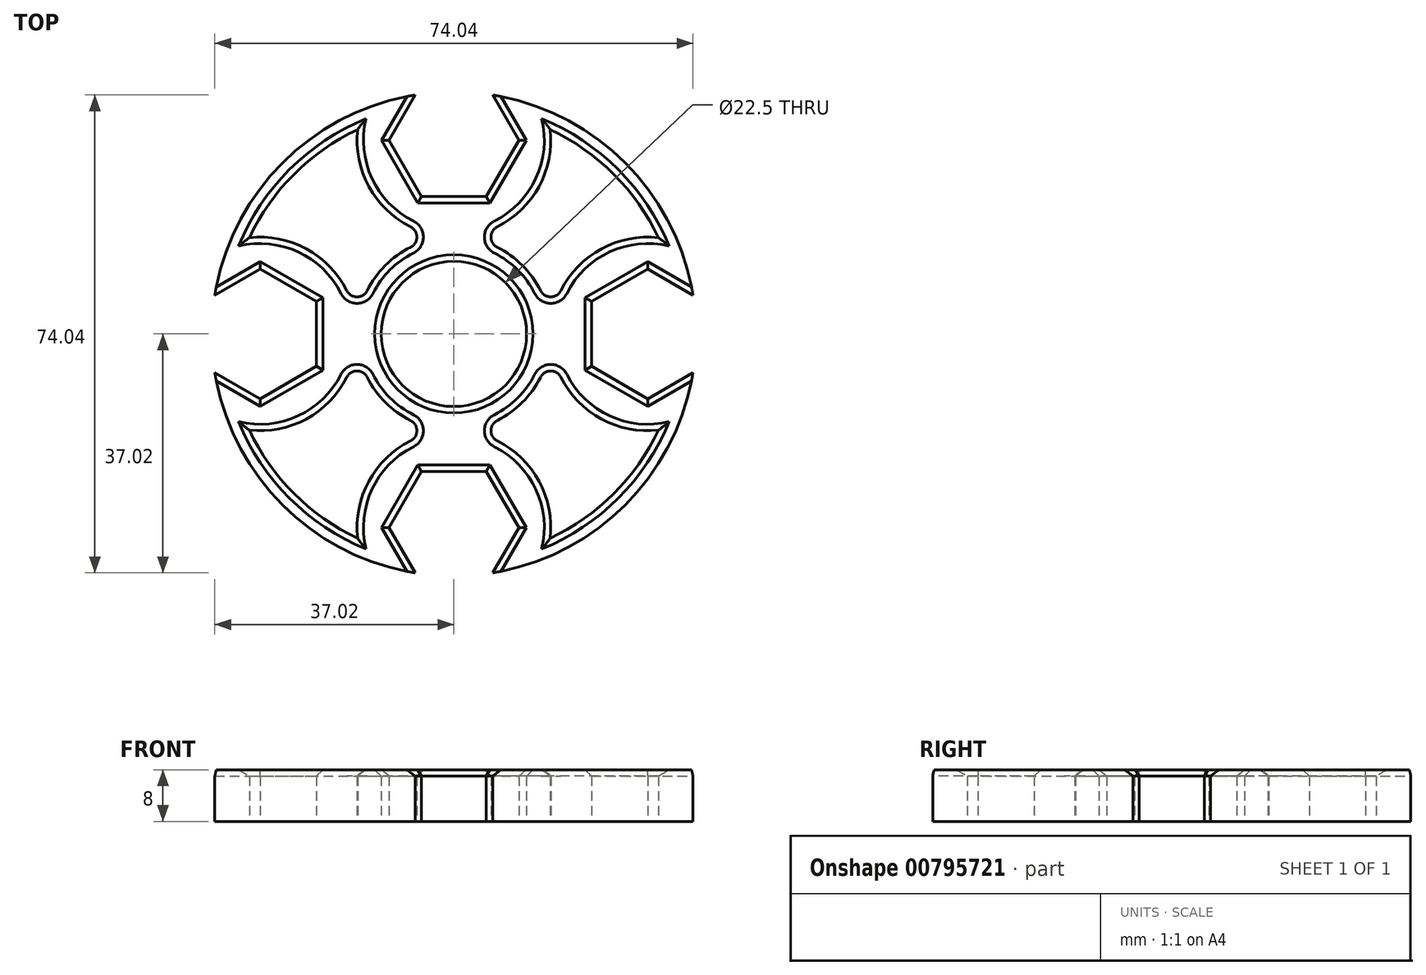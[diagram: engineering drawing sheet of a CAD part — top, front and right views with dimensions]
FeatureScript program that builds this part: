
annotation { "Feature Type Name" : "Feature", "Feature Type Description" : "" }
export const myFeature = defineFeature(function(context is Context, id is Id, definition is map)
    precondition{}
    {
        {
            var Q0;
            Q0=qCreatedBy(makeId("Top.planeOp"),FACE);
            var sketch = newSketch(context, id + "F0", { "sketchPlane" : qUnion([Q0])});
            skCircle(sketch, "E0", {"center": v(0, 0) * mm, "radius": 35 * mm});
            skLineSegment(sketch, "E1.bottom", {"start": v(-35, 35) * mm, "end": v(35, 35) * mm});
            skLineSegment(sketch, "E1.top", {"start": v(-35, -35) * mm, "end": v(35, -35) * mm});
            skLineSegment(sketch, "E1.left", {"start": v(-35, 35) * mm, "end": v(-35, -35) * mm});
            skLineSegment(sketch, "E1.right", {"start": v(35, 35) * mm, "end": v(35, -35) * mm});
            skCircle(sketch, "E2", {"center": v(0, 0) * mm, "radius": 15 * mm});
            skLineSegment(sketch, "E3", {"start": v(-35, 0) * mm, "end": v(-15, 0) * mm});
            skLineSegment(sketch, "E4", {"start": v(0, -15) * mm, "end": v(0, -35) * mm});
            skLineSegment(sketch, "E5", {"start": v(35, 0) * mm, "end": v(15, 0) * mm});
            skLineSegment(sketch, "E6", {"start": v(0, 35) * mm, "end": v(0, 15) * mm});
            skLineSegment(sketch, "E7", {"start": v(-25, 0) * mm, "end": v(-35, 0) * mm});
            skLineSegment(sketch, "E8", {"start": v(35, 0) * mm, "end": v(25, 0) * mm});
            skLineSegment(sketch, "E9", {"start": v(0, 35) * mm, "end": v(0, 25) * mm});
            skLineSegment(sketch, "E10", {"start": v(0, -25) * mm, "end": v(0, -35) * mm});
            skCircle(sketch, "E11.cCircle", {"center": v(-30, 0) * mm, "radius": 10.05 * mm, "construction": true});
            skPoint(sketch, "E11.cCircle.perimeterSnap0", {"position": v(-30, 0) * mm});
            skLineSegment(sketch, "E11.0", {"start": v(-30, 10.05) * mm, "end": v(-21.3, 5.02) * mm});
            skPoint(sketch, "E11.0.startSnap0", {"position": v(-30, 0) * mm});
            skLineSegment(sketch, "E11.1", {"start": v(-21.3, 5.03) * mm, "end": v(-21.3, -5.02) * mm});
            skLineSegment(sketch, "E11.2", {"start": v(-21.3, -5.02) * mm, "end": v(-30, -10.05) * mm});
            skLineSegment(sketch, "E11.3", {"start": v(-30, -10.05) * mm, "end": v(-38.7, -5.02) * mm});
            skLineSegment(sketch, "E11.4", {"start": v(-38.7, -5.03) * mm, "end": v(-38.7, 5.02) * mm});
            skLineSegment(sketch, "E11.5", {"start": v(-38.7, 5.02) * mm, "end": v(-30, 10.05) * mm});
            skCircle(sketch, "E12.cCircle", {"center": v(30, 0) * mm, "radius": 10.05 * mm, "construction": true});
            skPoint(sketch, "E12.cCircle.perimeterSnap0", {"position": v(30, 0) * mm});
            skLineSegment(sketch, "E12.0", {"start": v(30, 10.05) * mm, "end": v(38.7, 5.02) * mm});
            skPoint(sketch, "E12.0.startSnap0", {"position": v(30, 0) * mm});
            skLineSegment(sketch, "E12.1", {"start": v(38.7, 5.03) * mm, "end": v(38.7, -5.03) * mm});
            skLineSegment(sketch, "E12.2", {"start": v(38.7, -5.03) * mm, "end": v(30, -10.05) * mm});
            skLineSegment(sketch, "E12.3", {"start": v(30, -10.05) * mm, "end": v(21.3, -5.03) * mm});
            skLineSegment(sketch, "E12.4", {"start": v(21.3, -5.03) * mm, "end": v(21.3, 5.03) * mm});
            skLineSegment(sketch, "E12.5", {"start": v(21.3, 5.03) * mm, "end": v(30, 10.05) * mm});
            skCircle(sketch, "E13.cCircle", {"center": v(0, 30) * mm, "radius": 10.05 * mm, "construction": true});
            skPoint(sketch, "E13.cCircle.perimeterSnap0", {"position": v(0, 30) * mm});
            skLineSegment(sketch, "E13.0", {"start": v(10.05, 30) * mm, "end": v(5.03, 21.3) * mm});
            skPoint(sketch, "E13.0.startSnap0", {"position": v(0, 30) * mm});
            skLineSegment(sketch, "E13.1", {"start": v(5.03, 21.3) * mm, "end": v(-5.02, 21.3) * mm});
            skLineSegment(sketch, "E13.2", {"start": v(-5.02, 21.3) * mm, "end": v(-10.05, 30) * mm});
            skLineSegment(sketch, "E13.3", {"start": v(-10.05, 30) * mm, "end": v(-5.02, 38.7) * mm});
            skLineSegment(sketch, "E13.4", {"start": v(-5.02, 38.7) * mm, "end": v(5.03, 38.7) * mm});
            skLineSegment(sketch, "E13.5", {"start": v(5.03, 38.7) * mm, "end": v(10.05, 30) * mm});
            skCircle(sketch, "E14.cCircle", {"center": v(0, -30) * mm, "radius": 10.05 * mm, "construction": true});
            skPoint(sketch, "E14.cCircle.perimeterSnap0", {"position": v(0, -30) * mm});
            skLineSegment(sketch, "E14.0", {"start": v(10.05, -30) * mm, "end": v(5.03, -38.7) * mm});
            skPoint(sketch, "E14.0.startSnap0", {"position": v(0, -30) * mm});
            skLineSegment(sketch, "E14.1", {"start": v(5.03, -38.7) * mm, "end": v(-5.03, -38.7) * mm});
            skLineSegment(sketch, "E14.2", {"start": v(-5.03, -38.7) * mm, "end": v(-10.05, -30) * mm});
            skLineSegment(sketch, "E14.3", {"start": v(-10.05, -30) * mm, "end": v(-5.03, -21.3) * mm});
            skLineSegment(sketch, "E14.4", {"start": v(-5.03, -21.3) * mm, "end": v(5.02, -21.3) * mm});
            skLineSegment(sketch, "E14.5", {"start": v(5.02, -21.3) * mm, "end": v(10.05, -30) * mm});
            skCircle(sketch, "E15", {"center": v(0, 30) * mm, "radius": 15 * mm});
            skCircle(sketch, "E16", {"center": v(-30, 0) * mm, "radius": 15 * mm});
            skCircle(sketch, "E17", {"center": v(0, -30) * mm, "radius": 15 * mm});
            skCircle(sketch, "E18", {"center": v(30, 0) * mm, "radius": 15 * mm});
            skLineSegment(sketch, "E19", {"start": v(-15, 0) * mm, "end": v(-15, 7.5) * mm});
            skArc(sketch, "E20", {"start": v(-16.58, 6.7) * mm, "mid": v(-15, 5.73) * mm, "end": v(-13.42, 6.7) * mm});
            skLineSegment(sketch, "E21", {"start": v(-15, 0) * mm, "end": v(-15, -7.5) * mm});
            skLineSegment(sketch, "E22", {"start": v(15, 0) * mm, "end": v(15, 7.5) * mm});
            skLineSegment(sketch, "E23", {"start": v(15, 0) * mm, "end": v(15, -7.5) * mm});
            skLineSegment(sketch, "E24", {"start": v(0, 15) * mm, "end": v(-7.5, 15) * mm});
            skLineSegment(sketch, "E25", {"start": v(0, 15) * mm, "end": v(7.5, 15) * mm});
            skLineSegment(sketch, "E26", {"start": v(0, -15) * mm, "end": v(-7.5, -15) * mm});
            skLineSegment(sketch, "E27", {"start": v(0, -15) * mm, "end": v(7.5, -15) * mm});
            skArc(sketch, "E28", {"start": v(6.7, -13.42) * mm, "mid": v(5.73, -15) * mm, "end": v(6.7, -16.58) * mm});
            skArc(sketch, "E29", {"start": v(-6.7, -16.58) * mm, "mid": v(-5.73, -15) * mm, "end": v(-6.7, -13.42) * mm});
            skArc(sketch, "E30", {"start": v(-6.7, 13.42) * mm, "mid": v(-5.73, 15) * mm, "end": v(-6.7, 16.58) * mm});
            skArc(sketch, "E31", {"start": v(-13.42, -6.7) * mm, "mid": v(-15, -5.73) * mm, "end": v(-16.58, -6.7) * mm});
            skArc(sketch, "E32", {"start": v(16.58, -6.7) * mm, "mid": v(15, -5.73) * mm, "end": v(13.42, -6.7) * mm});
            skArc(sketch, "E33", {"start": v(13.42, 6.7) * mm, "mid": v(15, 5.73) * mm, "end": v(16.58, 6.7) * mm});
            skArc(sketch, "E34", {"start": v(6.7, 16.58) * mm, "mid": v(5.73, 15) * mm, "end": v(6.7, 13.42) * mm});
            skCircle(sketch, "E35", {"center": v(0, 0) * mm, "radius": 37.5 * mm});
            skCircle(sketch, "E36", {"center": v(0, 0) * mm, "radius": 11.25 * mm});
            skSolve(sketch);
        }
        {
            var Q0;
            {var subQ1=sQuery(id+"F0.wireOp",EDGE,"E11.0");Q0=makeQuery(id+"F0.imprint","IMPRINT",FACE,{"disambiguationData":[TD([[makeQuery(id+"F0.imprint","IMPRINT",EDGE,{"derivedFrom":subQ1}),1.0]])]});}
            var Q1;
            {var subQ0=sQuery(id+"F0.wireOp",EDGE,"E11.2");Q1=makeQuery(id+"F0.imprint","IMPRINT",FACE,{"disambiguationData":[TD([[makeQuery(id+"F0.imprint","IMPRINT",EDGE,{"derivedFrom":subQ0}),1.0]])]});}
            var Q2;
            {var subQ1=sQuery(id+"F0.wireOp",EDGE,"E0");var subQ5=sQuery(id+"F0.wireOp",EDGE,"E11.3");var subQ6=makeQuery(id+"F0.imprint","INTERSECT",VERTEX,{"derivedFrom":[subQ1,subQ5]});Q2=makeQuery(id+"F0.imprint","IMPRINT",FACE,{"disambiguationData":[TD([[makeQuery(id+"F0.imprint","IMPRINT",EDGE,{"disambiguationData":[TD([[subQ6,-1.0]])],"derivedFrom":subQ1}),-1.0]])]});}
            var Q3;
            {var subQ0=sQuery(id+"F0.wireOp",EDGE,"E11.3");var subQ1=sQuery(id+"F0.wireOp",EDGE,"E1.left");var subQ2=makeQuery(id+"F0.imprint","INTERSECT",VERTEX,{"derivedFrom":[subQ1,subQ0]});Q3=makeQuery(id+"F0.imprint","IMPRINT",FACE,{"disambiguationData":[TD([[makeQuery(id+"F0.imprint","IMPRINT",EDGE,{"disambiguationData":[TD([[subQ2,-1.0]])],"derivedFrom":subQ1}),-1.0]])]});}
            var Q4;
            {var subQ0=sQuery(id+"F0.wireOp",EDGE,"E35");var subQ1=sQuery(id+"F0.wireOp",EDGE,"E1.left");var subQ2=makeQuery(id+"F0.imprint","INTERSECT",VERTEX,{"disambiguationData":[OD(0.0)],"derivedFrom":[subQ1,subQ0]});Q4=makeQuery(id+"F0.imprint","IMPRINT",FACE,{"disambiguationData":[TD([[makeQuery(id+"F0.imprint","IMPRINT",EDGE,{"disambiguationData":[TD([[subQ2,-1.0]])],"derivedFrom":subQ1}),-1.0]])]});}
            var Q5;
            {var subQ0=sQuery(id+"F0.wireOp",EDGE,"E16");var subQ1=sQuery(id+"F0.wireOp",EDGE,"E0");var subQ2=makeQuery(id+"F0.imprint","INTERSECT",VERTEX,{"disambiguationData":[OD(0.0)],"derivedFrom":[subQ1,subQ0]});Q5=makeQuery(id+"F0.imprint","IMPRINT",FACE,{"disambiguationData":[TD([[makeQuery(id+"F0.imprint","IMPRINT",EDGE,{"disambiguationData":[TD([[subQ2,-1.0]])],"derivedFrom":subQ1}),-1.0]])]});}
            var Q6;
            {var subQ0=sQuery(id+"F0.wireOp",EDGE,"E15");var subQ1=sQuery(id+"F0.wireOp",EDGE,"E0");var subQ2=makeQuery(id+"F0.imprint","INTERSECT",VERTEX,{"disambiguationData":[OD(1.0)],"derivedFrom":[subQ1,subQ0]});Q6=makeQuery(id+"F0.imprint","IMPRINT",FACE,{"disambiguationData":[TD([[makeQuery(id+"F0.imprint","IMPRINT",EDGE,{"disambiguationData":[TD([[subQ2,-1.0]])],"derivedFrom":subQ1}),-1.0]])]});}
            var Q7;
            {var subQ0=sQuery(id+"F0.wireOp",EDGE,"E16");var subQ1=sQuery(id+"F0.wireOp",EDGE,"E0");var subQ2=makeQuery(id+"F0.imprint","INTERSECT",VERTEX,{"disambiguationData":[OD(1.0)],"derivedFrom":[subQ1,subQ0]});Q7=makeQuery(id+"F0.imprint","IMPRINT",FACE,{"disambiguationData":[TD([[makeQuery(id+"F0.imprint","IMPRINT",EDGE,{"disambiguationData":[TD([[subQ2,-1.0]])],"derivedFrom":subQ1}),-1.0]])]});}
            var Q8;
            {var subQ1=sQuery(id+"F0.wireOp",EDGE,"E16");var subQ3=sQuery(id+"F0.wireOp",EDGE,"E31");var subQ4=makeQuery(id+"F0.imprint","INTERSECT",VERTEX,{"derivedFrom":[subQ1,subQ3]});Q8=makeQuery(id+"F0.imprint","IMPRINT",FACE,{"disambiguationData":[TD([[makeQuery(id+"F0.imprint","IMPRINT",EDGE,{"disambiguationData":[TD([[subQ4,1.0]])],"derivedFrom":subQ3}),-1.0]])]});}
            var Q9;
            {var subQ1=sQuery(id+"F0.wireOp",EDGE,"E2");var subQ3=sQuery(id+"F0.wireOp",EDGE,"E31");var subQ4=makeQuery(id+"F0.imprint","INTERSECT",VERTEX,{"derivedFrom":[subQ1,subQ3]});Q9=makeQuery(id+"F0.imprint","IMPRINT",FACE,{"disambiguationData":[TD([[makeQuery(id+"F0.imprint","IMPRINT",EDGE,{"disambiguationData":[TD([[subQ4,-1.0]])],"derivedFrom":subQ3}),-1.0]])]});}
            var Q10;
            {var subQ1=sQuery(id+"F0.wireOp",EDGE,"E16");var subQ3=sQuery(id+"F0.wireOp",EDGE,"E20");var subQ4=makeQuery(id+"F0.imprint","INTERSECT",VERTEX,{"derivedFrom":[subQ1,subQ3]});Q10=makeQuery(id+"F0.imprint","IMPRINT",FACE,{"disambiguationData":[TD([[makeQuery(id+"F0.imprint","IMPRINT",EDGE,{"disambiguationData":[TD([[subQ4,-1.0]])],"derivedFrom":subQ3}),-1.0]])]});}
            var Q11;
            {var subQ1=sQuery(id+"F0.wireOp",EDGE,"E2");var subQ3=sQuery(id+"F0.wireOp",EDGE,"E20");var subQ4=makeQuery(id+"F0.imprint","INTERSECT",VERTEX,{"derivedFrom":[subQ1,subQ3]});Q11=makeQuery(id+"F0.imprint","IMPRINT",FACE,{"disambiguationData":[TD([[makeQuery(id+"F0.imprint","IMPRINT",EDGE,{"disambiguationData":[TD([[subQ4,1.0]])],"derivedFrom":subQ3}),-1.0]])]});}
            var Q12;
            {var subQ0=sQuery(id+"F0.wireOp",EDGE,"E14.3");Q12=makeQuery(id+"F0.imprint","IMPRINT",FACE,{"disambiguationData":[TD([[makeQuery(id+"F0.imprint","IMPRINT",EDGE,{"derivedFrom":subQ0}),1.0]])]});}
            var Q13;
            {var subQ0=sQuery(id+"F0.wireOp",EDGE,"E17");var subQ1=sQuery(id+"F0.wireOp",EDGE,"E0");var subQ2=makeQuery(id+"F0.imprint","INTERSECT",VERTEX,{"disambiguationData":[OD(0.0)],"derivedFrom":[subQ1,subQ0]});Q13=makeQuery(id+"F0.imprint","IMPRINT",FACE,{"disambiguationData":[TD([[makeQuery(id+"F0.imprint","IMPRINT",EDGE,{"disambiguationData":[TD([[subQ2,-1.0]])],"derivedFrom":subQ1}),-1.0]])]});}
            var Q14;
            {var subQ0=sQuery(id+"F0.wireOp",EDGE,"E35");var subQ1=sQuery(id+"F0.wireOp",EDGE,"E1.top");var subQ2=makeQuery(id+"F0.imprint","INTERSECT",VERTEX,{"disambiguationData":[OD(0.0)],"derivedFrom":[subQ1,subQ0]});Q14=makeQuery(id+"F0.imprint","IMPRINT",FACE,{"disambiguationData":[TD([[makeQuery(id+"F0.imprint","IMPRINT",EDGE,{"disambiguationData":[TD([[subQ2,-1.0]])],"derivedFrom":subQ1}),-1.0]])]});}
            var Q15;
            {var subQ0=sQuery(id+"F0.wireOp",EDGE,"E14.0");var subQ1=sQuery(id+"F0.wireOp",EDGE,"E1.top");var subQ2=makeQuery(id+"F0.imprint","INTERSECT",VERTEX,{"derivedFrom":[subQ1,subQ0]});Q15=makeQuery(id+"F0.imprint","IMPRINT",FACE,{"disambiguationData":[TD([[makeQuery(id+"F0.imprint","IMPRINT",EDGE,{"disambiguationData":[TD([[subQ2,-1.0]])],"derivedFrom":subQ1}),-1.0]])]});}
            var Q16;
            {var subQ1=sQuery(id+"F0.wireOp",EDGE,"E0");var subQ5=sQuery(id+"F0.wireOp",EDGE,"E14.0");var subQ9=makeQuery(id+"F0.imprint","INTERSECT",VERTEX,{"derivedFrom":[subQ1,subQ5]});Q16=makeQuery(id+"F0.imprint","IMPRINT",FACE,{"disambiguationData":[TD([[makeQuery(id+"F0.imprint","IMPRINT",EDGE,{"disambiguationData":[TD([[subQ9,-1.0]])],"derivedFrom":subQ1}),-1.0]])]});}
            var Q17;
            {var subQ0=sQuery(id+"F0.wireOp",EDGE,"E14.5");Q17=makeQuery(id+"F0.imprint","IMPRINT",FACE,{"disambiguationData":[TD([[makeQuery(id+"F0.imprint","IMPRINT",EDGE,{"derivedFrom":subQ0}),1.0]])]});}
            var Q18;
            {var subQ0=sQuery(id+"F0.wireOp",EDGE,"E17");var subQ1=sQuery(id+"F0.wireOp",EDGE,"E0");var subQ2=makeQuery(id+"F0.imprint","INTERSECT",VERTEX,{"disambiguationData":[OD(1.0)],"derivedFrom":[subQ1,subQ0]});Q18=makeQuery(id+"F0.imprint","IMPRINT",FACE,{"disambiguationData":[TD([[makeQuery(id+"F0.imprint","IMPRINT",EDGE,{"disambiguationData":[TD([[subQ2,-1.0]])],"derivedFrom":subQ1}),-1.0]])]});}
            var Q19;
            {var subQ0=sQuery(id+"F0.wireOp",EDGE,"E18");var subQ1=sQuery(id+"F0.wireOp",EDGE,"E0");var subQ2=makeQuery(id+"F0.imprint","INTERSECT",VERTEX,{"disambiguationData":[OD(1.0)],"derivedFrom":[subQ1,subQ0]});Q19=makeQuery(id+"F0.imprint","IMPRINT",FACE,{"disambiguationData":[TD([[makeQuery(id+"F0.imprint","IMPRINT",EDGE,{"disambiguationData":[TD([[subQ2,-1.0]])],"derivedFrom":subQ1}),-1.0]])]});}
            var Q20;
            {var subQ0=sQuery(id+"F0.wireOp",EDGE,"E12.2");var subQ1=sQuery(id+"F0.wireOp",EDGE,"E1.right");var subQ2=makeQuery(id+"F0.imprint","INTERSECT",VERTEX,{"derivedFrom":[subQ1,subQ0]});Q20=makeQuery(id+"F0.imprint","IMPRINT",FACE,{"disambiguationData":[TD([[makeQuery(id+"F0.imprint","IMPRINT",EDGE,{"disambiguationData":[TD([[subQ2,-1.0]])],"derivedFrom":subQ1}),1.0]])]});}
            var Q21;
            {var subQ0=sQuery(id+"F0.wireOp",EDGE,"E12.3");Q21=makeQuery(id+"F0.imprint","IMPRINT",FACE,{"disambiguationData":[TD([[makeQuery(id+"F0.imprint","IMPRINT",EDGE,{"derivedFrom":subQ0}),1.0]])]});}
            var Q22;
            {var subQ0=sQuery(id+"F0.wireOp",EDGE,"E12.5");Q22=makeQuery(id+"F0.imprint","IMPRINT",FACE,{"disambiguationData":[TD([[makeQuery(id+"F0.imprint","IMPRINT",EDGE,{"derivedFrom":subQ0}),1.0]])]});}
            var Q23;
            {var subQ0=sQuery(id+"F0.wireOp",EDGE,"E12.0");var subQ1=sQuery(id+"F0.wireOp",EDGE,"E0");var subQ2=makeQuery(id+"F0.imprint","INTERSECT",VERTEX,{"derivedFrom":[subQ1,subQ0]});Q23=makeQuery(id+"F0.imprint","IMPRINT",FACE,{"disambiguationData":[TD([[makeQuery(id+"F0.imprint","IMPRINT",EDGE,{"disambiguationData":[TD([[subQ2,-1.0]])],"derivedFrom":subQ1}),-1.0]])]});}
            var Q24;
            {var subQ0=sQuery(id+"F0.wireOp",EDGE,"E35");var subQ1=sQuery(id+"F0.wireOp",EDGE,"E1.right");var subQ2=makeQuery(id+"F0.imprint","INTERSECT",VERTEX,{"disambiguationData":[OD(0.0)],"derivedFrom":[subQ1,subQ0]});Q24=makeQuery(id+"F0.imprint","IMPRINT",FACE,{"disambiguationData":[TD([[makeQuery(id+"F0.imprint","IMPRINT",EDGE,{"disambiguationData":[TD([[subQ2,-1.0]])],"derivedFrom":subQ1}),1.0]])]});}
            var Q25;
            {var subQ0=sQuery(id+"F0.wireOp",EDGE,"E18");var subQ1=sQuery(id+"F0.wireOp",EDGE,"E0");var subQ2=makeQuery(id+"F0.imprint","INTERSECT",VERTEX,{"disambiguationData":[OD(0.0)],"derivedFrom":[subQ1,subQ0]});Q25=makeQuery(id+"F0.imprint","IMPRINT",FACE,{"disambiguationData":[TD([[makeQuery(id+"F0.imprint","IMPRINT",EDGE,{"disambiguationData":[TD([[subQ2,-1.0]])],"derivedFrom":subQ1}),-1.0]])]});}
            var Q26;
            {var subQ5=sQuery(id+"F0.wireOp",EDGE,"E0");var subQ7=sQuery(id+"F0.wireOp",EDGE,"E15");var subQ8=makeQuery(id+"F0.imprint","INTERSECT",VERTEX,{"disambiguationData":[OD(0.0)],"derivedFrom":[subQ5,subQ7]});Q26=makeQuery(id+"F0.imprint","IMPRINT",FACE,{"disambiguationData":[TD([[makeQuery(id+"F0.imprint","IMPRINT",EDGE,{"disambiguationData":[TD([[subQ8,-1.0]])],"derivedFrom":subQ5}),-1.0]])]});}
            var Q27;
            {var subQ0=sQuery(id+"F0.wireOp",EDGE,"E13.5");var subQ1=sQuery(id+"F0.wireOp",EDGE,"E1.bottom");var subQ2=makeQuery(id+"F0.imprint","INTERSECT",VERTEX,{"derivedFrom":[subQ1,subQ0]});Q27=makeQuery(id+"F0.imprint","IMPRINT",FACE,{"disambiguationData":[TD([[makeQuery(id+"F0.imprint","IMPRINT",EDGE,{"disambiguationData":[TD([[subQ2,-1.0]])],"derivedFrom":subQ1}),1.0]])]});}
            var Q28;
            {var subQ0=sQuery(id+"F0.wireOp",EDGE,"E13.0");Q28=makeQuery(id+"F0.imprint","IMPRINT",FACE,{"disambiguationData":[TD([[makeQuery(id+"F0.imprint","IMPRINT",EDGE,{"derivedFrom":subQ0}),1.0]])]});}
            var Q29;
            {var subQ0=sQuery(id+"F0.wireOp",EDGE,"E13.2");Q29=makeQuery(id+"F0.imprint","IMPRINT",FACE,{"disambiguationData":[TD([[makeQuery(id+"F0.imprint","IMPRINT",EDGE,{"derivedFrom":subQ0}),1.0]])]});}
            var Q30;
            {var subQ1=sQuery(id+"F0.wireOp",EDGE,"E0");var subQ7=sQuery(id+"F0.wireOp",EDGE,"E13.3");var subQ9=makeQuery(id+"F0.imprint","INTERSECT",VERTEX,{"derivedFrom":[subQ1,subQ7]});Q30=makeQuery(id+"F0.imprint","IMPRINT",FACE,{"disambiguationData":[TD([[makeQuery(id+"F0.imprint","IMPRINT",EDGE,{"disambiguationData":[TD([[subQ9,-1.0]])],"derivedFrom":subQ1}),-1.0]])]});}
            var Q31;
            {var subQ0=sQuery(id+"F0.wireOp",EDGE,"E35");var subQ1=sQuery(id+"F0.wireOp",EDGE,"E1.bottom");var subQ2=makeQuery(id+"F0.imprint","INTERSECT",VERTEX,{"disambiguationData":[OD(0.0)],"derivedFrom":[subQ1,subQ0]});Q31=makeQuery(id+"F0.imprint","IMPRINT",FACE,{"disambiguationData":[TD([[makeQuery(id+"F0.imprint","IMPRINT",EDGE,{"disambiguationData":[TD([[subQ2,-1.0]])],"derivedFrom":subQ1}),1.0]])]});}
            var Q32;
            {var subQ1=sQuery(id+"F0.wireOp",EDGE,"E2");var subQ3=sQuery(id+"F0.wireOp",EDGE,"E30");var subQ4=makeQuery(id+"F0.imprint","INTERSECT",VERTEX,{"derivedFrom":[subQ1,subQ3]});Q32=makeQuery(id+"F0.imprint","IMPRINT",FACE,{"disambiguationData":[TD([[makeQuery(id+"F0.imprint","IMPRINT",EDGE,{"disambiguationData":[TD([[subQ4,-1.0]])],"derivedFrom":subQ3}),-1.0]])]});}
            var Q33;
            {var subQ1=sQuery(id+"F0.wireOp",EDGE,"E15");var subQ3=sQuery(id+"F0.wireOp",EDGE,"E30");var subQ4=makeQuery(id+"F0.imprint","INTERSECT",VERTEX,{"derivedFrom":[subQ1,subQ3]});Q33=makeQuery(id+"F0.imprint","IMPRINT",FACE,{"disambiguationData":[TD([[makeQuery(id+"F0.imprint","IMPRINT",EDGE,{"disambiguationData":[TD([[subQ4,1.0]])],"derivedFrom":subQ3}),-1.0]])]});}
            var Q34;
            {var subQ1=sQuery(id+"F0.wireOp",EDGE,"E15");var subQ3=sQuery(id+"F0.wireOp",EDGE,"E34");var subQ4=makeQuery(id+"F0.imprint","INTERSECT",VERTEX,{"derivedFrom":[subQ1,subQ3]});Q34=makeQuery(id+"F0.imprint","IMPRINT",FACE,{"disambiguationData":[TD([[makeQuery(id+"F0.imprint","IMPRINT",EDGE,{"disambiguationData":[TD([[subQ4,-1.0]])],"derivedFrom":subQ3}),-1.0]])]});}
            var Q35;
            {var subQ1=sQuery(id+"F0.wireOp",EDGE,"E2");var subQ3=sQuery(id+"F0.wireOp",EDGE,"E34");var subQ4=makeQuery(id+"F0.imprint","INTERSECT",VERTEX,{"derivedFrom":[subQ1,subQ3]});Q35=makeQuery(id+"F0.imprint","IMPRINT",FACE,{"disambiguationData":[TD([[makeQuery(id+"F0.imprint","IMPRINT",EDGE,{"disambiguationData":[TD([[subQ4,1.0]])],"derivedFrom":subQ3}),-1.0]])]});}
            var Q36;
            {var subQ1=sQuery(id+"F0.wireOp",EDGE,"E18");var subQ3=sQuery(id+"F0.wireOp",EDGE,"E33");var subQ4=makeQuery(id+"F0.imprint","INTERSECT",VERTEX,{"derivedFrom":[subQ1,subQ3]});Q36=makeQuery(id+"F0.imprint","IMPRINT",FACE,{"disambiguationData":[TD([[makeQuery(id+"F0.imprint","IMPRINT",EDGE,{"disambiguationData":[TD([[subQ4,1.0]])],"derivedFrom":subQ3}),-1.0]])]});}
            var Q37;
            {var subQ1=sQuery(id+"F0.wireOp",EDGE,"E2");var subQ3=sQuery(id+"F0.wireOp",EDGE,"E33");var subQ4=makeQuery(id+"F0.imprint","INTERSECT",VERTEX,{"derivedFrom":[subQ1,subQ3]});Q37=makeQuery(id+"F0.imprint","IMPRINT",FACE,{"disambiguationData":[TD([[makeQuery(id+"F0.imprint","IMPRINT",EDGE,{"disambiguationData":[TD([[subQ4,-1.0]])],"derivedFrom":subQ3}),-1.0]])]});}
            var Q38;
            {var subQ1=sQuery(id+"F0.wireOp",EDGE,"E2");var subQ3=sQuery(id+"F0.wireOp",EDGE,"E32");var subQ4=makeQuery(id+"F0.imprint","INTERSECT",VERTEX,{"derivedFrom":[subQ1,subQ3]});Q38=makeQuery(id+"F0.imprint","IMPRINT",FACE,{"disambiguationData":[TD([[makeQuery(id+"F0.imprint","IMPRINT",EDGE,{"disambiguationData":[TD([[subQ4,1.0]])],"derivedFrom":subQ3}),-1.0]])]});}
            var Q39;
            {var subQ1=sQuery(id+"F0.wireOp",EDGE,"E2");var subQ3=sQuery(id+"F0.wireOp",EDGE,"E28");var subQ4=makeQuery(id+"F0.imprint","INTERSECT",VERTEX,{"derivedFrom":[subQ1,subQ3]});Q39=makeQuery(id+"F0.imprint","IMPRINT",FACE,{"disambiguationData":[TD([[makeQuery(id+"F0.imprint","IMPRINT",EDGE,{"disambiguationData":[TD([[subQ4,-1.0]])],"derivedFrom":subQ3}),-1.0]])]});}
            var Q40;
            {var subQ1=sQuery(id+"F0.wireOp",EDGE,"E17");var subQ3=sQuery(id+"F0.wireOp",EDGE,"E28");var subQ4=makeQuery(id+"F0.imprint","INTERSECT",VERTEX,{"derivedFrom":[subQ1,subQ3]});Q40=makeQuery(id+"F0.imprint","IMPRINT",FACE,{"disambiguationData":[TD([[makeQuery(id+"F0.imprint","IMPRINT",EDGE,{"disambiguationData":[TD([[subQ4,1.0]])],"derivedFrom":subQ3}),-1.0]])]});}
            var Q41;
            {var subQ1=sQuery(id+"F0.wireOp",EDGE,"E18");var subQ3=sQuery(id+"F0.wireOp",EDGE,"E32");var subQ4=makeQuery(id+"F0.imprint","INTERSECT",VERTEX,{"derivedFrom":[subQ1,subQ3]});Q41=makeQuery(id+"F0.imprint","IMPRINT",FACE,{"disambiguationData":[TD([[makeQuery(id+"F0.imprint","IMPRINT",EDGE,{"disambiguationData":[TD([[subQ4,-1.0]])],"derivedFrom":subQ3}),-1.0]])]});}
            var Q42;
            Q42=makeQuery(id+"F0.imprint","IMPRINT",FACE,{"disambiguationData":[TD([[makeQuery(id+"F0.imprint","IMPRINT",EDGE,{"derivedFrom":sQuery(id+"F0.wireOp",EDGE,"E36")}),-1.0]])]});
            var Q43;
            {var subQ1=sQuery(id+"F0.wireOp",EDGE,"E17");var subQ3=sQuery(id+"F0.wireOp",EDGE,"E29");var subQ4=makeQuery(id+"F0.imprint","INTERSECT",VERTEX,{"derivedFrom":[subQ1,subQ3]});Q43=makeQuery(id+"F0.imprint","IMPRINT",FACE,{"disambiguationData":[TD([[makeQuery(id+"F0.imprint","IMPRINT",EDGE,{"disambiguationData":[TD([[subQ4,-1.0]])],"derivedFrom":subQ3}),-1.0]])]});}
            var Q44;
            {var subQ1=sQuery(id+"F0.wireOp",EDGE,"E2");var subQ3=sQuery(id+"F0.wireOp",EDGE,"E29");var subQ4=makeQuery(id+"F0.imprint","INTERSECT",VERTEX,{"derivedFrom":[subQ1,subQ3]});Q44=makeQuery(id+"F0.imprint","IMPRINT",FACE,{"disambiguationData":[TD([[makeQuery(id+"F0.imprint","IMPRINT",EDGE,{"disambiguationData":[TD([[subQ4,1.0]])],"derivedFrom":subQ3}),-1.0]])]});}
            extrude(context, id + "F1", {"entities" : qUnion([Q0, Q1, Q2, Q3, Q4, Q5, Q6, Q7, Q8, Q9, Q10, Q11, Q12, Q13, Q14, Q15, Q16, Q17, Q18, Q19, Q20, Q21, Q22, Q23, Q24, Q25, Q26, Q27, Q28, Q29, Q30, Q31, Q32, Q33, Q34, Q35, Q36, Q37, Q38, Q39, Q40, Q41, Q42, Q43, Q44]), "depth" : 8 * mm, "offsetDistance" : 25 * mm});
        }
        {
            var Q0;
            Q0=makeQuery(id+"F1.opExtrude","CAP_EDGE",EDGE,{"disambiguationData":[OSD([sQuery(id+"F0.wireOp",EDGE,"E36")])],"isStart":false});
            var Q1;
            Q1=makeQuery(id+"F1.opExtrude","CAP_EDGE",EDGE,{"disambiguationData":[OSD([sQuery(id+"F0.wireOp",EDGE,"E13.3")])],"isStart":false});
            var Q2;
            Q2=makeQuery(id+"F1.opExtrude","CAP_EDGE",EDGE,{"disambiguationData":[OSD([sQuery(id+"F0.wireOp",EDGE,"E13.2")])],"isStart":false});
            var Q3;
            Q3=makeQuery(id+"F1.opExtrude","CAP_EDGE",EDGE,{"disambiguationData":[OSD([sQuery(id+"F0.wireOp",EDGE,"E13.1")])],"isStart":false});
            var Q4;
            Q4=makeQuery(id+"F1.opExtrude","CAP_EDGE",EDGE,{"disambiguationData":[OSD([sQuery(id+"F0.wireOp",EDGE,"E13.0")])],"isStart":false});
            var Q5;
            Q5=makeQuery(id+"F1.opExtrude","CAP_EDGE",EDGE,{"disambiguationData":[OSD([sQuery(id+"F0.wireOp",EDGE,"E13.5")])],"isStart":false});
            var Q6;
            Q6=makeQuery(id+"F1.opExtrude","CAP_EDGE",EDGE,{"disambiguationData":[OSD([sQuery(id+"F0.wireOp",EDGE,"E12.5")])],"isStart":false});
            var Q7;
            Q7=makeQuery(id+"F1.opExtrude","CAP_EDGE",EDGE,{"disambiguationData":[OSD([sQuery(id+"F0.wireOp",EDGE,"E12.0")])],"isStart":false});
            var Q8;
            Q8=makeQuery(id+"F1.opExtrude","CAP_EDGE",EDGE,{"disambiguationData":[OSD([sQuery(id+"F0.wireOp",EDGE,"E12.4")])],"isStart":false});
            var Q9;
            Q9=makeQuery(id+"F1.opExtrude","CAP_EDGE",EDGE,{"disambiguationData":[OSD([sQuery(id+"F0.wireOp",EDGE,"E12.3")])],"isStart":false});
            var Q10;
            Q10=makeQuery(id+"F1.opExtrude","CAP_EDGE",EDGE,{"disambiguationData":[OSD([sQuery(id+"F0.wireOp",EDGE,"E12.2")])],"isStart":false});
            var Q11;
            {var subQ0=sQuery(id+"F0.wireOp",EDGE,"E18");Q11=makeQuery(id+"F1.opExtrude","CAP_EDGE",EDGE,{"disambiguationData":[OSD([subQ0]),TDD([makeQuery(id+"F0.imprint","IMPRINT",EDGE,{"disambiguationData":[TD([[makeQuery(id+"F0.imprint","INTERSECT",VERTEX,{"derivedFrom":[subQ0,sQuery(id+"F0.wireOp",EDGE,"E32")]}),-1.0]])],"derivedFrom":subQ0})])],"isStart":false});}
            var Q12;
            {var subQ0=sQuery(id+"F0.wireOp",EDGE,"E15");Q12=makeQuery(id+"F1.opExtrude","CAP_EDGE",EDGE,{"disambiguationData":[OSD([subQ0]),TDD([makeQuery(id+"F0.imprint","IMPRINT",EDGE,{"disambiguationData":[TD([[makeQuery(id+"F0.imprint","INTERSECT",VERTEX,{"derivedFrom":[subQ0,sQuery(id+"F0.wireOp",EDGE,"E34")]}),-1.0]])],"derivedFrom":subQ0})])],"isStart":false});}
            var Q13;
            {var subQ0=sQuery(id+"F0.wireOp",EDGE,"E0");Q13=makeQuery(id+"F1.opExtrude","CAP_EDGE",EDGE,{"disambiguationData":[OSD([subQ0]),TDD([makeQuery(id+"F0.imprint","IMPRINT",EDGE,{"disambiguationData":[TD([[makeQuery(id+"F0.imprint","INTERSECT",VERTEX,{"disambiguationData":[OD(1.0)],"derivedFrom":[subQ0,sQuery(id+"F0.wireOp",EDGE,"E17")]}),-1.0]])],"derivedFrom":subQ0})])],"isStart":false});}
            var Q14;
            {var subQ0=sQuery(id+"F0.wireOp",EDGE,"E0");Q14=makeQuery(id+"F1.opExtrude","CAP_EDGE",EDGE,{"disambiguationData":[OSD([subQ0]),TDD([makeQuery(id+"F0.imprint","IMPRINT",EDGE,{"disambiguationData":[TD([[makeQuery(id+"F0.imprint","INTERSECT",VERTEX,{"disambiguationData":[OD(0.0)],"derivedFrom":[subQ0,sQuery(id+"F0.wireOp",EDGE,"E18")]}),-1.0]])],"derivedFrom":subQ0})])],"isStart":false});}
            var Q15;
            Q15=makeQuery(id+"F1.opExtrude","CAP_EDGE",EDGE,{"disambiguationData":[OSD([sQuery(id+"F0.wireOp",EDGE,"E14.0")])],"isStart":false});
            var Q16;
            Q16=makeQuery(id+"F1.opExtrude","CAP_EDGE",EDGE,{"disambiguationData":[OSD([sQuery(id+"F0.wireOp",EDGE,"E14.5")])],"isStart":false});
            var Q17;
            Q17=makeQuery(id+"F1.opExtrude","CAP_EDGE",EDGE,{"disambiguationData":[OSD([sQuery(id+"F0.wireOp",EDGE,"E14.4")])],"isStart":false});
            var Q18;
            Q18=makeQuery(id+"F1.opExtrude","CAP_EDGE",EDGE,{"disambiguationData":[OSD([sQuery(id+"F0.wireOp",EDGE,"E14.3")])],"isStart":false});
            var Q19;
            Q19=makeQuery(id+"F1.opExtrude","CAP_EDGE",EDGE,{"disambiguationData":[OSD([sQuery(id+"F0.wireOp",EDGE,"E14.2")])],"isStart":false});
            var Q20;
            {var subQ0=sQuery(id+"F0.wireOp",EDGE,"E16");Q20=makeQuery(id+"F1.opExtrude","CAP_EDGE",EDGE,{"disambiguationData":[OSD([subQ0]),TDD([makeQuery(id+"F0.imprint","IMPRINT",EDGE,{"disambiguationData":[TD([[makeQuery(id+"F0.imprint","INTERSECT",VERTEX,{"derivedFrom":[subQ0,sQuery(id+"F0.wireOp",EDGE,"E31")]}),1.0]])],"derivedFrom":subQ0})])],"isStart":false});}
            var Q21;
            {var subQ0=sQuery(id+"F0.wireOp",EDGE,"E0");Q21=makeQuery(id+"F1.opExtrude","CAP_EDGE",EDGE,{"disambiguationData":[OSD([subQ0]),TDD([makeQuery(id+"F0.imprint","IMPRINT",EDGE,{"disambiguationData":[TD([[makeQuery(id+"F0.imprint","INTERSECT",VERTEX,{"disambiguationData":[OD(1.0)],"derivedFrom":[subQ0,sQuery(id+"F0.wireOp",EDGE,"E16")]}),-1.0]])],"derivedFrom":subQ0})])],"isStart":false});}
            var Q22;
            Q22=makeQuery(id+"F1.opExtrude","CAP_EDGE",EDGE,{"disambiguationData":[OSD([sQuery(id+"F0.wireOp",EDGE,"E11.3")])],"isStart":false});
            var Q23;
            Q23=makeQuery(id+"F1.opExtrude","CAP_EDGE",EDGE,{"disambiguationData":[OSD([sQuery(id+"F0.wireOp",EDGE,"E11.2")])],"isStart":false});
            var Q24;
            Q24=makeQuery(id+"F1.opExtrude","CAP_EDGE",EDGE,{"disambiguationData":[OSD([sQuery(id+"F0.wireOp",EDGE,"E11.1")])],"isStart":false});
            var Q25;
            Q25=makeQuery(id+"F1.opExtrude","CAP_EDGE",EDGE,{"disambiguationData":[OSD([sQuery(id+"F0.wireOp",EDGE,"E11.0")])],"isStart":false});
            var Q26;
            Q26=makeQuery(id+"F1.opExtrude","CAP_EDGE",EDGE,{"disambiguationData":[OSD([sQuery(id+"F0.wireOp",EDGE,"E11.5")])],"isStart":false});
            var Q27;
            {var subQ0=sQuery(id+"F0.wireOp",EDGE,"E16");Q27=makeQuery(id+"F1.opExtrude","CAP_EDGE",EDGE,{"disambiguationData":[OSD([subQ0]),TDD([makeQuery(id+"F0.imprint","IMPRINT",EDGE,{"disambiguationData":[TD([[makeQuery(id+"F0.imprint","INTERSECT",VERTEX,{"derivedFrom":[subQ0,sQuery(id+"F0.wireOp",EDGE,"E20")]}),-1.0]])],"derivedFrom":subQ0})])],"isStart":false});}
            var Q28;
            {var subQ0=sQuery(id+"F0.wireOp",EDGE,"E0");Q28=makeQuery(id+"F1.opExtrude","CAP_EDGE",EDGE,{"disambiguationData":[OSD([subQ0]),TDD([makeQuery(id+"F0.imprint","IMPRINT",EDGE,{"disambiguationData":[TD([[makeQuery(id+"F0.imprint","INTERSECT",VERTEX,{"disambiguationData":[OD(1.0)],"derivedFrom":[subQ0,sQuery(id+"F0.wireOp",EDGE,"E15")]}),-1.0]])],"derivedFrom":subQ0})])],"isStart":false});}
            chamfer(context, id + "F2", {"entities" : qUnion([Q0, Q1, Q2, Q3, Q4, Q5, Q6, Q7, Q8, Q9, Q10, Q11, Q12, Q13, Q14, Q15, Q16, Q17, Q18, Q19, Q20, Q21, Q22, Q23, Q24, Q25, Q26, Q27, Q28]), "width" : 1 * mm, "tangentPropagation" : true});
        }
    });
